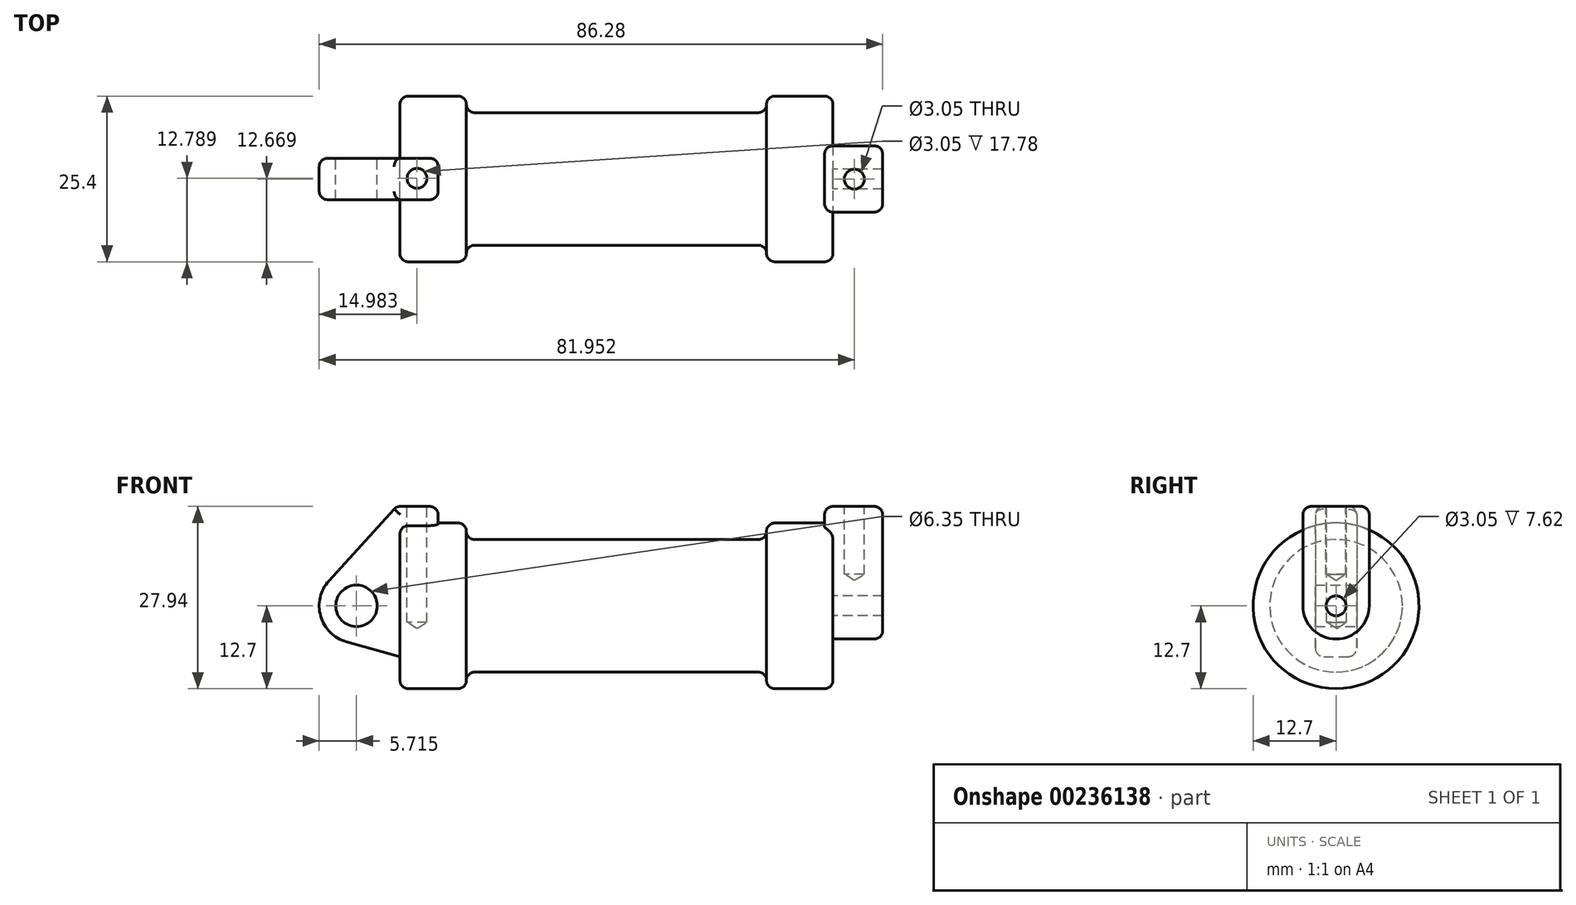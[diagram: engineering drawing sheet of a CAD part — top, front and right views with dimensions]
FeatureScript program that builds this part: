
annotation { "Feature Type Name" : "Feature", "Feature Type Description" : "" }
export const myFeature = defineFeature(function(context is Context, id is Id, definition is map)
    precondition{}
    {
        {
            var Q0;
            Q0=qCreatedBy(makeId("Front.planeOp"),FACE);
            var sketch = newSketch(context, id + "F0", { "sketchPlane" : qUnion([Q0])});
            skLineSegment(sketch, "E0", {"start": v(0, 0) * mm, "end": v(0, 12.7) * mm});
            skLineSegment(sketch, "E1", {"start": v(0, 12.7) * mm, "end": v(10.16, 12.7) * mm});
            skLineSegment(sketch, "E2", {"start": v(10.16, 12.7) * mm, "end": v(10.16, 10.16) * mm});
            skLineSegment(sketch, "E3", {"start": v(10.16, 10.16) * mm, "end": v(56.13, 10.16) * mm});
            skLineSegment(sketch, "E4", {"start": v(56.13, 10.16) * mm, "end": v(56.13, 12.7) * mm});
            skLineSegment(sketch, "E5", {"start": v(56.13, 12.7) * mm, "end": v(66.3, 12.7) * mm});
            skLineSegment(sketch, "E6", {"start": v(66.3, 12.7) * mm, "end": v(66.3, 0) * mm});
            skLineSegment(sketch, "E7", {"start": v(66.3, 0) * mm, "end": v(0, 0) * mm});
            skLineSegment(sketch, "E8", {"start": v(5.84, 15.24) * mm, "end": v(-0.5, 15.24) * mm});
            skLineSegment(sketch, "E9", {"start": v(-0.5, 15.24) * mm, "end": v(-10.88, 3.85) * mm});
            skLineSegment(sketch, "E10", {"start": v(0, 0) * mm, "end": v(-6.65, 0) * mm});
            skCircle(sketch, "E11", {"center": v(-6.65, 0) * mm, "radius": 5.72 * mm});
            skCircle(sketch, "E12", {"center": v(-6.65, 0) * mm, "radius": 3.18 * mm});
            skLineSegment(sketch, "E13", {"start": v(5.84, 15.24) * mm, "end": v(5.84, -9.4) * mm});
            skLineSegment(sketch, "E14", {"start": v(5.84, -9.4) * mm, "end": v(-8.18, -5.5) * mm});
            skSolve(sketch);
        }
        {
            var Q0;
            {var subQ0=sQuery(id+"F0.wireOp",EDGE,"E0");Q0=makeQuery(id+"F0.imprint","IMPRINT",FACE,{"disambiguationData":[TD([[makeQuery(id+"F0.imprint","IMPRINT",EDGE,{"derivedFrom":subQ0}),-1.0]])]});}
            var Q1;
            {var subQ0=sQuery(id+"F0.wireOp",EDGE,"E2");Q1=makeQuery(id+"F0.imprint","IMPRINT",FACE,{"disambiguationData":[TD([[makeQuery(id+"F0.imprint","IMPRINT",EDGE,{"derivedFrom":subQ0}),-1.0]])]});}
            var Q2;
            Q2=sQuery(id+"F0.wireOp",EDGE,"E7");
            revolve(context, id + "F1", {"entities" : qUnion([Q0, Q1]), "axis" : qUnion([Q2]), "revolveType" : RevolveType.FULL});
        }
        {
            var Q0;
            {var subQ0=sQuery(id+"F0.wireOp",EDGE,"E0");Q0=makeQuery(id+"F0.imprint","IMPRINT",FACE,{"disambiguationData":[TD([[makeQuery(id+"F0.imprint","IMPRINT",EDGE,{"derivedFrom":subQ0}),-1.0]])]});}
            var Q1;
            {var subQ3=sQuery(id+"F0.wireOp",EDGE,"E0");Q1=makeQuery(id+"F0.imprint","IMPRINT",FACE,{"disambiguationData":[TD([[makeQuery(id+"F0.imprint","IMPRINT",EDGE,{"derivedFrom":subQ3}),1.0]])]});}
            var Q2;
            {var subQ0=sQuery(id+"F0.wireOp",EDGE,"E14");Q2=makeQuery(id+"F0.imprint","IMPRINT",FACE,{"disambiguationData":[TD([[makeQuery(id+"F0.imprint","IMPRINT",EDGE,{"derivedFrom":subQ0}),-1.0]])]});}
            var Q3;
            {var subQ4=sQuery(id+"F0.wireOp",EDGE,"E12");Q3=makeQuery(id+"F0.imprint","IMPRINT",FACE,{"disambiguationData":[TD([[makeQuery(id+"F0.imprint","IMPRINT",EDGE,{"derivedFrom":subQ4}),-1.0]])]});}
            extrude(context, id + "F2", {"entities" : qUnion([Q0, Q1, Q2, Q3]), "operationType" : NewBodyOperationType.ADD, "endBound" : BoundingType.SYMMETRIC, "depth" : 6.35 * mm});
        }
        {
            var Q0;
            Q0=makeQuery(id+"F1.opRevolve","SWEPT_FACE",FACE,{"disambiguationData":[OSD([sQuery(id+"F0.wireOp",EDGE,"E6")])]});
            var sketch = newSketch(context, id + "F3", { "sketchPlane" : qUnion([Q0])});
            skCircle(sketch, "E15", {"center": v(0, 0) * mm, "radius": 1.52 * mm});
            skCircle(sketch, "E16", {"center": v(0, 0) * mm, "radius": 5.08 * mm});
            skLineSegment(sketch, "E17", {"start": v(5.08, 0) * mm, "end": v(5.08, 15.24) * mm});
            skLineSegment(sketch, "E18", {"start": v(-5.08, 0) * mm, "end": v(-5.08, 15.24) * mm});
            skLineSegment(sketch, "E19", {"start": v(-5.08, 15.24) * mm, "end": v(5.08, 15.24) * mm});
            skSolve(sketch);
        }
        {
            var Q0;
            Q0=makeQuery(id+"F3.imprint","IMPRINT",FACE,{"disambiguationData":[TD([[makeQuery(id+"F3.imprint","IMPRINT",EDGE,{"derivedFrom":sQuery(id+"F3.wireOp",EDGE,"E15")}),-1.0]])]});
            var Q1;
            {var subQ0=sQuery(id+"F3.wireOp",EDGE,"E17");var subQ1=sQuery(id+"F3.wireOp",EDGE,"E16");var subQ2=makeQuery(id+"F3.imprint","INTERSECT",VERTEX,{"derivedFrom":[subQ1,subQ0]});Q1=makeQuery(id+"F3.imprint","IMPRINT",FACE,{"disambiguationData":[TD([[makeQuery(id+"F3.imprint","IMPRINT",EDGE,{"disambiguationData":[TD([[subQ2,-1.0]])],"derivedFrom":subQ1}),-1.0]])]});}
            var Q2;
            {var subQ0=sQuery(id+"F3.wireOp",EDGE,"E19");Q2=makeQuery(id+"F3.imprint","IMPRINT",FACE,{"disambiguationData":[TD([[makeQuery(id+"F3.imprint","IMPRINT",EDGE,{"derivedFrom":subQ0}),-1.0]])]});}
            extrude(context, id + "F4", {"entities" : qUnion([Q0, Q1, Q2]), "operationType" : NewBodyOperationType.ADD, "depth" : 7.62 * mm});
        }
        {
            var Q0;
            Q0=makeQuery(id+"F4.opExtrude","CAP_FACE",FACE,{"disambiguationData":[OSD([sQuery(id+"F3.wireOp",EDGE,"E15"),sQuery(id+"F3.wireOp",EDGE,"E16"),sQuery(id+"F3.wireOp",EDGE,"E17"),sQuery(id+"F3.wireOp",EDGE,"E18"),sQuery(id+"F3.wireOp",EDGE,"E19")])],"isStart":true});
            extrude(context, id + "F5", {"entities" : qUnion([Q0]), "operationType" : NewBodyOperationType.ADD, "depth" : 1.27 * mm});
        }
        {
            var Q0;
            {var subQ0=sQuery(id+"F3.wireOp",EDGE,"E19");Q0=makeQuery(id+"F5.boolean.opBoolean","MERGE",FACE,{"derivedFrom":[makeQuery(id+"F4.opExtrude","SWEPT_FACE",FACE,{"disambiguationData":[OSD([subQ0])]}),makeQuery(id+"F5.opExtrude","SWEPT_FACE",FACE,{"disambiguationData":[OSD([subQ0])]})]});}
            var sketch = newSketch(context, id + "F6", { "sketchPlane" : qUnion([Q0])});
            skPoint(sketch, "E20", {"position": v(69.58, -0.03) * mm});
            skSolve(sketch);
        }
        {
            var Q0;
            Q0=sQuery(id+"F6.wireOp",VERTEX,"E20");
            var Q1;
            Q1=makeQuery(id+"F1.opRevolve","SWEPT_BODY",BODY,{"disambiguationData":[OSD([sQuery(id+"F0.wireOp",EDGE,"E0"),sQuery(id+"F0.wireOp",EDGE,"E1"),sQuery(id+"F0.wireOp",EDGE,"E2"),sQuery(id+"F0.wireOp",EDGE,"E3"),sQuery(id+"F0.wireOp",EDGE,"E4"),sQuery(id+"F0.wireOp",EDGE,"E5"),sQuery(id+"F0.wireOp",EDGE,"E6"),sQuery(id+"F0.wireOp",EDGE,"E7")])]});
            hole(context, id + "F7", {"style" : HoleStyle.SIMPLE, "endStyle" : HoleEndStyle.BLIND, "holeDiameter" : 3.05 * mm, "holeDepth" : 10.4 * mm, "locations" : qUnion([Q0]), "scope" : qUnion([Q1])});
        }
        {
            var Q0;
            Q0=makeQuery(id+"F2.opExtrude","SWEPT_FACE",FACE,{"disambiguationData":[OSD([sQuery(id+"F0.wireOp",EDGE,"E8")])]});
            var sketch = newSketch(context, id + "F8", { "sketchPlane" : qUnion([Q0])});
            skPoint(sketch, "E21", {"position": v(2.61, 0.09) * mm});
            skSolve(sketch);
        }
        {
            var Q0;
            Q0=sQuery(id+"F8.wireOp",VERTEX,"E21");
            var Q1;
            Q1=makeQuery(id+"F1.opRevolve","SWEPT_BODY",BODY,{"disambiguationData":[OSD([sQuery(id+"F0.wireOp",EDGE,"E0"),sQuery(id+"F0.wireOp",EDGE,"E1"),sQuery(id+"F0.wireOp",EDGE,"E2"),sQuery(id+"F0.wireOp",EDGE,"E3"),sQuery(id+"F0.wireOp",EDGE,"E4"),sQuery(id+"F0.wireOp",EDGE,"E5"),sQuery(id+"F0.wireOp",EDGE,"E6"),sQuery(id+"F0.wireOp",EDGE,"E7")])]});
            hole(context, id + "F9", {"style" : HoleStyle.SIMPLE, "endStyle" : HoleEndStyle.BLIND, "holeDiameter" : 3.05 * mm, "holeDepth" : 17.78 * mm, "locations" : qUnion([Q0]), "scope" : qUnion([Q1])});
        }
        {
            var Q0;
            Q0=makeQuery(id+"F1.opRevolve","SWEPT_EDGE",EDGE,{"disambiguationData":[OSD([sQuery(id+"F0.wireOp",EDGE,"E1"),sQuery(id+"F0.wireOp",EDGE,"E2")])]});
            var Q1;
            Q1=makeQuery(id+"F1.opRevolve","SWEPT_EDGE",EDGE,{"disambiguationData":[OSD([sQuery(id+"F0.wireOp",EDGE,"E2"),sQuery(id+"F0.wireOp",EDGE,"E3")])]});
            var Q2;
            Q2=makeQuery(id+"F1.opRevolve","SWEPT_EDGE",EDGE,{"disambiguationData":[OSD([sQuery(id+"F0.wireOp",EDGE,"E3"),sQuery(id+"F0.wireOp",EDGE,"E4")])]});
            var Q3;
            Q3=makeQuery(id+"F1.opRevolve","SWEPT_EDGE",EDGE,{"disambiguationData":[OSD([sQuery(id+"F0.wireOp",EDGE,"E4"),sQuery(id+"F0.wireOp",EDGE,"E5")])]});
            fillet(context, id + "F10", {"entities" : qUnion([Q0, Q1, Q2, Q3]), "radius" : 1.27 * mm, "tangentPropagation" : true, "allowEdgeOverflow" : false});
        }
        {
            var Q0;
            Q0=makeQuery(id+"F5.opExtrude","CAP_EDGE",EDGE,{"disambiguationData":[OSD([sQuery(id+"F3.wireOp",EDGE,"E19")])],"isStart":false});
            var Q1;
            {var subQ0=sQuery(id+"F3.wireOp",EDGE,"E19");var subQ1=sQuery(id+"F3.wireOp",EDGE,"E18");Q1=makeQuery(id+"F5.boolean.opBoolean","MERGE",EDGE,{"derivedFrom":[makeQuery(id+"F4.opExtrude","SWEPT_EDGE",EDGE,{"disambiguationData":[OSD([subQ1,subQ0])]}),makeQuery(id+"F5.opExtrude","SWEPT_EDGE",EDGE,{"disambiguationData":[OSD([subQ1,subQ0])]})]});}
            var Q2;
            Q2=makeQuery(id+"F4.opExtrude","CAP_EDGE",EDGE,{"disambiguationData":[OSD([sQuery(id+"F3.wireOp",EDGE,"E19")])],"isStart":false});
            var Q3;
            {var subQ0=sQuery(id+"F3.wireOp",EDGE,"E19");var subQ1=sQuery(id+"F3.wireOp",EDGE,"E17");Q3=makeQuery(id+"F5.boolean.opBoolean","MERGE",EDGE,{"derivedFrom":[makeQuery(id+"F4.opExtrude","SWEPT_EDGE",EDGE,{"disambiguationData":[OSD([subQ1,subQ0])]}),makeQuery(id+"F5.opExtrude","SWEPT_EDGE",EDGE,{"disambiguationData":[OSD([subQ1,subQ0])]})]});}
            var Q4;
            Q4=makeQuery(id+"F4.opExtrude","CAP_EDGE",EDGE,{"disambiguationData":[OSD([sQuery(id+"F3.wireOp",EDGE,"E18")])],"isStart":false});
            var Q5;
            Q5=makeQuery(id+"F4.opExtrude","CAP_EDGE",EDGE,{"disambiguationData":[OSD([sQuery(id+"F3.wireOp",EDGE,"E17")])],"isStart":false});
            var Q6;
            Q6=makeQuery(id+"F4.boolean.opBoolean","SPLIT",EDGE,{"disambiguationData":[OD(1.0)],"derivedFrom":makeQuery(id+"F1.opRevolve","SWEPT_EDGE",EDGE,{"disambiguationData":[OSD([sQuery(id+"F0.wireOp",EDGE,"E5"),sQuery(id+"F0.wireOp",EDGE,"E6")])]})});
            var Q7;
            Q7=makeQuery(id+"F1.opRevolve","SWEPT_EDGE",EDGE,{"disambiguationData":[OSD([sQuery(id+"F0.wireOp",EDGE,"E0"),sQuery(id+"F0.wireOp",EDGE,"E1")])]});
            var Q8;
            Q8=makeQuery(id+"F2.opExtrude","CAP_EDGE",EDGE,{"disambiguationData":[OSD([sQuery(id+"F0.wireOp",EDGE,"E8")])],"isStart":false});
            var Q9;
            Q9=makeQuery(id+"F2.opExtrude","SWEPT_EDGE",EDGE,{"disambiguationData":[OSD([sQuery(id+"F0.wireOp",EDGE,"E8"),sQuery(id+"F0.wireOp",EDGE,"E13")])]});
            var Q10;
            Q10=makeQuery(id+"F2.opExtrude","CAP_EDGE",EDGE,{"disambiguationData":[OSD([sQuery(id+"F0.wireOp",EDGE,"E8")])],"isStart":true});
            var Q11;
            Q11=makeQuery(id+"F2.opExtrude","CAP_EDGE",EDGE,{"disambiguationData":[OSD([sQuery(id+"F0.wireOp",EDGE,"E13")])],"isStart":true});
            var Q12;
            Q12=makeQuery(id+"F2.opExtrude","CAP_EDGE",EDGE,{"disambiguationData":[OSD([sQuery(id+"F0.wireOp",EDGE,"E13")])],"isStart":false});
            var Q13;
            Q13=makeQuery(id+"F2.opExtrude","CAP_EDGE",EDGE,{"disambiguationData":[OSD([sQuery(id+"F0.wireOp",EDGE,"E9")])],"isStart":false});
            var Q14;
            Q14=makeQuery(id+"F2.opExtrude","CAP_EDGE",EDGE,{"disambiguationData":[OSD([sQuery(id+"F0.wireOp",EDGE,"E9")])],"isStart":true});
            fillet(context, id + "F11", {"entities" : qUnion([Q0, Q1, Q2, Q3, Q4, Q5, Q6, Q7, Q8, Q9, Q10, Q11, Q12, Q13, Q14]), "radius" : 1.27 * mm, "tangentPropagation" : true, "allowEdgeOverflow" : false});
        }
        {
            var Q0;
            {var subQ0=sQuery(id+"F3.wireOp",EDGE,"E19");var subQ1=sQuery(id+"F3.wireOp",EDGE,"E17");Q0=makeQuery(id+"F11.opFillet","BLEND_EDGE",EDGE,{"blendedFrom":[makeQuery(id+"F5.opExtrude","CAP_EDGE",EDGE,{"disambiguationData":[OSD([subQ0])],"isStart":false}),makeQuery(id+"F5.boolean.opBoolean","MERGE",EDGE,{"derivedFrom":[makeQuery(id+"F4.opExtrude","SWEPT_EDGE",EDGE,{"disambiguationData":[OSD([subQ1,subQ0])]}),makeQuery(id+"F5.opExtrude","SWEPT_EDGE",EDGE,{"disambiguationData":[OSD([subQ1,subQ0])]})]})],"blendedInto":[]});}
            var Q1;
            {var subQ0=sQuery(id+"F3.wireOp",EDGE,"E19");var subQ1=sQuery(id+"F3.wireOp",EDGE,"E18");Q1=makeQuery(id+"F11.opFillet","BLEND_EDGE",EDGE,{"blendedFrom":[makeQuery(id+"F5.opExtrude","CAP_EDGE",EDGE,{"disambiguationData":[OSD([subQ0])],"isStart":false}),makeQuery(id+"F5.boolean.opBoolean","MERGE",EDGE,{"derivedFrom":[makeQuery(id+"F4.opExtrude","SWEPT_EDGE",EDGE,{"disambiguationData":[OSD([subQ1,subQ0])]}),makeQuery(id+"F5.opExtrude","SWEPT_EDGE",EDGE,{"disambiguationData":[OSD([subQ1,subQ0])]})]})],"blendedInto":[]});}
            var Q2;
            Q2=makeQuery(id+"F2.opExtrude","SWEPT_EDGE",EDGE,{"disambiguationData":[OSD([sQuery(id+"F0.wireOp",EDGE,"E8"),sQuery(id+"F0.wireOp",EDGE,"E9")])]});
            fillet(context, id + "F12", {"entities" : qUnion([Q0, Q1, Q2]), "radius" : 1.27 * mm, "tangentPropagation" : true, "allowEdgeOverflow" : false});
        }
    });
